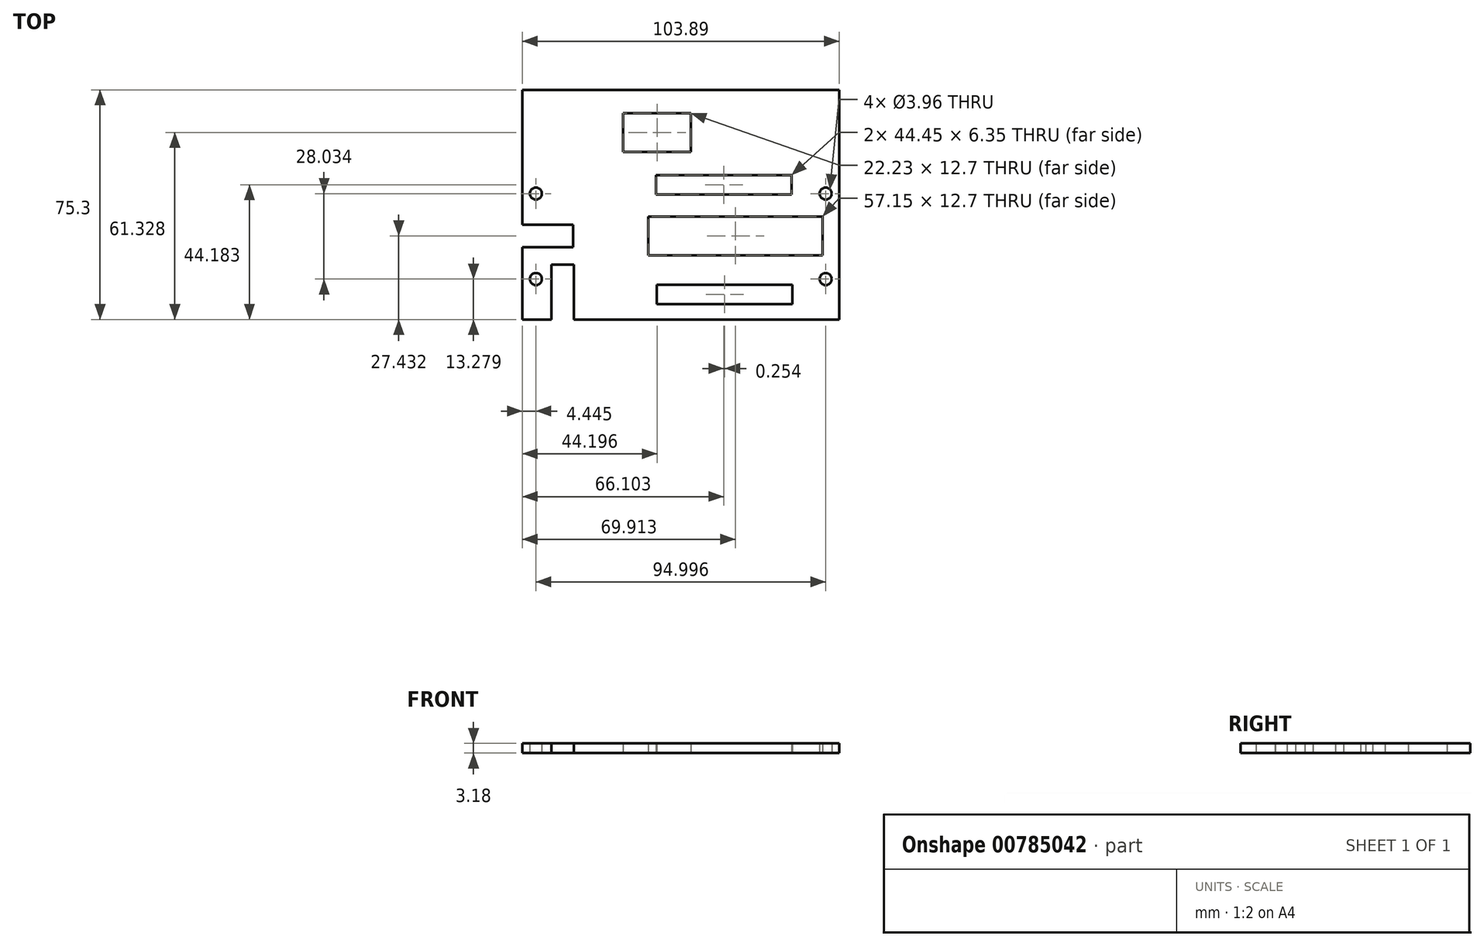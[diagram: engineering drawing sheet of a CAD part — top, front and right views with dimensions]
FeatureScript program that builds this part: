
annotation { "Feature Type Name" : "Feature", "Feature Type Description" : "" }
export const myFeature = defineFeature(function(context is Context, id is Id, definition is map)
    precondition{}
    {
        {
            var Q0;
            Q0=qCreatedBy(makeId("Top.planeOp"),FACE);
            var sketch = newSketch(context, id + "F0", { "sketchPlane" : qUnion([Q0])});
            skLineSegment(sketch, "E0.bottom", {"start": v(0, 0) * mm, "end": v(103.89, 0) * mm});
            skLineSegment(sketch, "E0.top", {"start": v(0, 75.3) * mm, "end": v(103.89, 75.3) * mm});
            skLineSegment(sketch, "E0.left", {"start": v(0, 0) * mm, "end": v(0, 75.3) * mm});
            skLineSegment(sketch, "E0.right", {"start": v(103.89, 0) * mm, "end": v(103.89, 75.3) * mm});
            skLineSegment(sketch, "E1.bottom", {"start": v(9.52, 0) * mm, "end": v(16.89, 0) * mm});
            skLineSegment(sketch, "E1.top", {"start": v(9.52, 18.03) * mm, "end": v(16.89, 18.03) * mm});
            skLineSegment(sketch, "E1.left", {"start": v(9.52, 0) * mm, "end": v(9.52, 18.03) * mm});
            skLineSegment(sketch, "E1.right", {"start": v(16.89, 0) * mm, "end": v(16.89, 18.03) * mm});
            skLineSegment(sketch, "E2.bottom", {"start": v(0, 31.1) * mm, "end": v(16.64, 31.1) * mm});
            skLineSegment(sketch, "E2.top", {"start": v(0, 23.74) * mm, "end": v(16.64, 23.74) * mm});
            skLineSegment(sketch, "E2.left", {"start": v(0, 31.1) * mm, "end": v(0, 23.74) * mm});
            skLineSegment(sketch, "E2.right", {"start": v(16.64, 31.1) * mm, "end": v(16.64, 23.74) * mm});
            skLineSegment(sketch, "E3.bottom", {"start": v(33.08, 67.68) * mm, "end": v(55.3, 67.68) * mm});
            skLineSegment(sketch, "E3.top", {"start": v(33.08, 54.98) * mm, "end": v(55.3, 54.98) * mm});
            skLineSegment(sketch, "E3.left", {"start": v(33.08, 67.68) * mm, "end": v(33.08, 54.98) * mm});
            skLineSegment(sketch, "E3.right", {"start": v(55.3, 67.68) * mm, "end": v(55.3, 54.98) * mm});
            skLineSegment(sketch, "E4.bottom", {"start": v(43.88, 47.36) * mm, "end": v(88.33, 47.36) * mm});
            skLineSegment(sketch, "E4.top", {"start": v(43.88, 41) * mm, "end": v(88.33, 41) * mm});
            skLineSegment(sketch, "E4.left", {"start": v(43.88, 47.36) * mm, "end": v(43.88, 41) * mm});
            skLineSegment(sketch, "E4.right", {"start": v(88.33, 47.36) * mm, "end": v(88.33, 41) * mm});
            skLineSegment(sketch, "E5.bottom", {"start": v(41.34, 33.78) * mm, "end": v(98.49, 33.78) * mm});
            skLineSegment(sketch, "E5.top", {"start": v(41.34, 21.08) * mm, "end": v(98.49, 21.08) * mm});
            skLineSegment(sketch, "E5.left", {"start": v(41.34, 33.78) * mm, "end": v(41.34, 21.08) * mm});
            skLineSegment(sketch, "E5.right", {"start": v(98.49, 33.78) * mm, "end": v(98.49, 21.08) * mm});
            skLineSegment(sketch, "E6.bottom", {"start": v(44.13, 11.43) * mm, "end": v(88.58, 11.43) * mm});
            skLineSegment(sketch, "E6.top", {"start": v(44.13, 5.08) * mm, "end": v(88.58, 5.08) * mm});
            skLineSegment(sketch, "E6.left", {"start": v(44.13, 11.43) * mm, "end": v(44.13, 5.08) * mm});
            skLineSegment(sketch, "E6.right", {"start": v(88.58, 11.43) * mm, "end": v(88.58, 5.08) * mm});
            skCircle(sketch, "E7", {"center": v(99.44, 13.28) * mm, "radius": 1.98 * mm});
            skCircle(sketch, "E8", {"center": v(99.44, 41.31) * mm, "radius": 1.98 * mm});
            skCircle(sketch, "E9", {"center": v(4.44, 41.31) * mm, "radius": 1.98 * mm});
            skCircle(sketch, "E10", {"center": v(4.45, 13.28) * mm, "radius": 1.98 * mm});
            skSolve(sketch);
        }
        {
            var Q0;
            {var subQ5=sQuery(id+"F0.wireOp",EDGE,"E0.top");Q0=makeQuery(id+"F0.imprint","IMPRINT",FACE,{"disambiguationData":[TD([[makeQuery(id+"F0.imprint","IMPRINT",EDGE,{"derivedFrom":subQ5}),-1.0]])]});}
            extrude(context, id + "F1", {"entities" : qUnion([Q0]), "depth" : 3.17 * mm, "offsetDistance" : 25.4 * mm});
        }
    });
